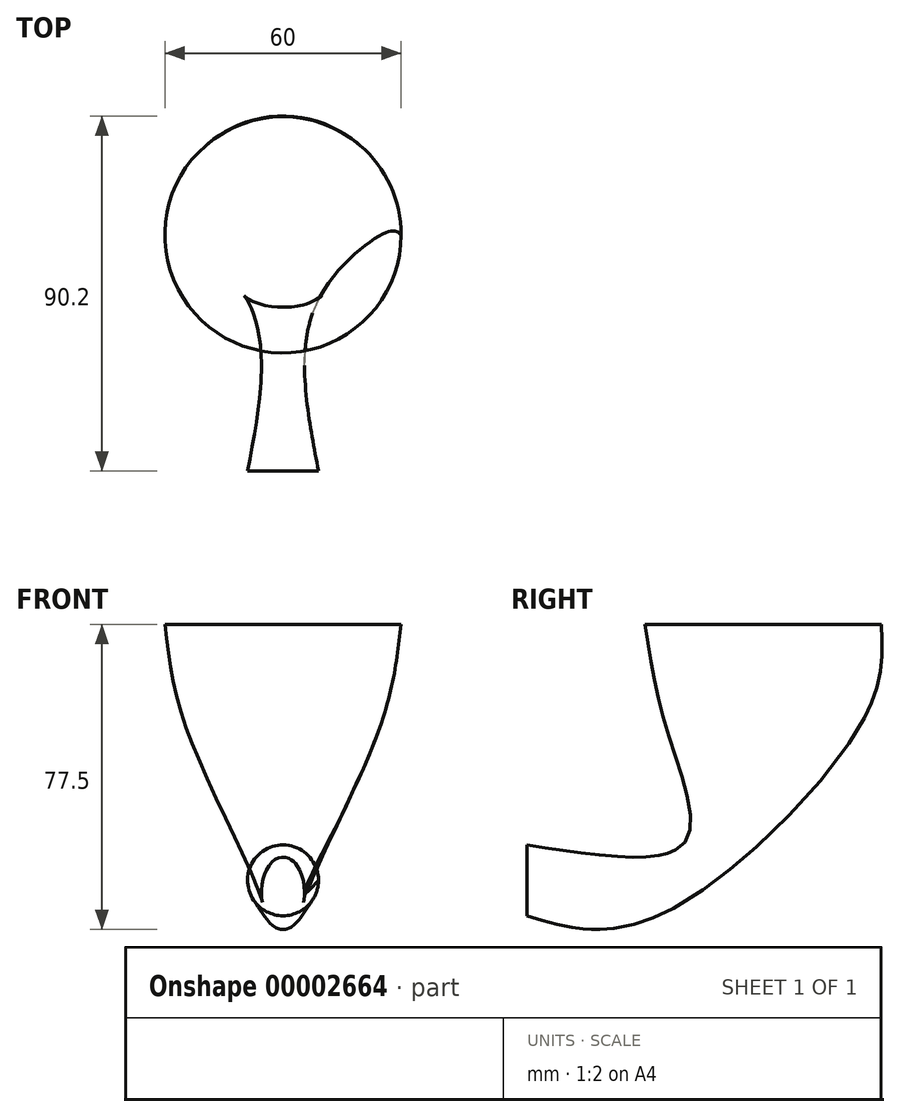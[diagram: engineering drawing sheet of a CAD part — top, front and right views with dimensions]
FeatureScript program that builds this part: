
annotation { "Feature Type Name" : "Feature", "Feature Type Description" : "" }
export const myFeature = defineFeature(function(context is Context, id is Id, definition is map)
    precondition{}
    {
        {
            var Q0;
            Q0=qCreatedBy(makeId("Top.planeOp"),FACE);
            var sketch = newSketch(context, id + "F0", { "sketchPlane" : qUnion([Q0])});
            skCircle(sketch, "E0", {"center": v(0, 60) * mm, "radius": 30 * mm});
            skLineSegment(sketch, "E1", {"start": v(-30, 60) * mm, "end": v(30, 60) * mm, "construction": true});
            skSolve(sketch);
        }
        {
            var Q0;
            Q0=qCreatedBy(makeId("Top.planeOp"),FACE);
            cPlane(context, id + "F1", {"entities" : qUnion([Q0]), "cplaneType" : CPlaneType.OFFSET, "offset" : 25 * mm, "oppositeDirection" : true, "width" : 150 * mm, "height" : 150 * mm});
        }
        {
            var Q0;
            Q0=qCreatedBy(id+"F1.planeOp",FACE);
            var sketch = newSketch(context, id + "F2", { "sketchPlane" : qUnion([Q0])});
            skCircle(sketch, "E2.0", {"center": v(0, 60) * mm, "radius": 25 * mm});
            skLineSegment(sketch, "E3", {"start": v(-25, 60) * mm, "end": v(25, 60) * mm, "construction": true});
            skSolve(sketch);
        }
        {
            var Q0;
            Q0=qCreatedBy(makeId("Front.planeOp"),FACE);
            cPlane(context, id + "F3", {"entities" : qUnion([Q0]), "cplaneType" : CPlaneType.OFFSET, "offset" : 40 * mm, "oppositeDirection" : true, "width" : 150 * mm, "height" : 150 * mm});
        }
        {
            var Q0;
            Q0=qCreatedBy(id+"F3.planeOp",FACE);
            var sketch = newSketch(context, id + "F4", { "sketchPlane" : qUnion([Q0])});
            skCircle(sketch, "E4.0", {"center": v(0, -63) * mm, "radius": 7.5 * mm});
            skLineSegment(sketch, "E5", {"start": v(-7.5, -63) * mm, "end": v(7.5, -63) * mm, "construction": true});
            skSolve(sketch);
        }
        {
            var Q0;
            Q0=qCreatedBy(makeId("Front.planeOp"),FACE);
            var sketch = newSketch(context, id + "F5", { "sketchPlane" : qUnion([Q0])});
            skCircle(sketch, "E6", {"center": v(0, -65) * mm, "radius": 9 * mm});
            skLineSegment(sketch, "E7", {"start": v(-9, -65) * mm, "end": v(9, -65) * mm, "construction": true});
            skSolve(sketch);
        }
        {
            var Q0;
            Q0=makeQuery(id+"F0.imprint","IMPRINT",FACE,{"disambiguationData":[TD([[makeQuery(id+"F0.imprint","IMPRINT",EDGE,{"derivedFrom":sQuery(id+"F0.wireOp",EDGE,"E0")}),1.0]])]});
            var Q1;
            Q1=makeQuery(id+"F5.imprint","IMPRINT",FACE,{"disambiguationData":[TD([[makeQuery(id+"F5.imprint","IMPRINT",EDGE,{"derivedFrom":sQuery(id+"F5.wireOp",EDGE,"E6")}),1.0]])]});
            var Q2;
            Q2=sQuery(id+"F0.wireOp",EDGE,"E0");
            var Q3;
            Q3=sQuery(id+"F2.wireOp",EDGE,"E2.0");
            var Q4;
            Q4=sQuery(id+"F4.wireOp",EDGE,"E4.0");
            var Q5;
            Q5=sQuery(id+"F5.wireOp",EDGE,"E6");
            var Q6;
            Q6=sQuery(id+"F0.wireOp",VERTEX,"E1.end");
            var Q7;
            Q7=sQuery(id+"F2.wireOp",VERTEX,"E3.end");
            var Q8;
            Q8=sQuery(id+"F4.wireOp",VERTEX,"E5.end");
            var Q9;
            Q9=sQuery(id+"F5.wireOp",VERTEX,"E7.end");
            loft(context, id + "F6", {"bodyType" : ToolBodyType.SURFACE, "sheetProfilesArray" : [{ "sheetProfileEntities" : qUnion([Q0]) }, { "sheetProfileEntities" : qUnion([Q1]) }], "wireProfilesArray" : [{ "wireProfileEntities" : qUnion([Q2]) }, { "wireProfileEntities" : qUnion([Q3]) }, { "wireProfileEntities" : qUnion([Q4]) }, { "wireProfileEntities" : qUnion([Q5]) }], "matchConnections" : true, "connections" : [{ "connectionEntities" : qUnion([Q6, Q7, Q8, Q9]), "connectionEdgeQueries" : qUnion([]), "connectionEdgeParameters" : [] }]});
        }
    });
